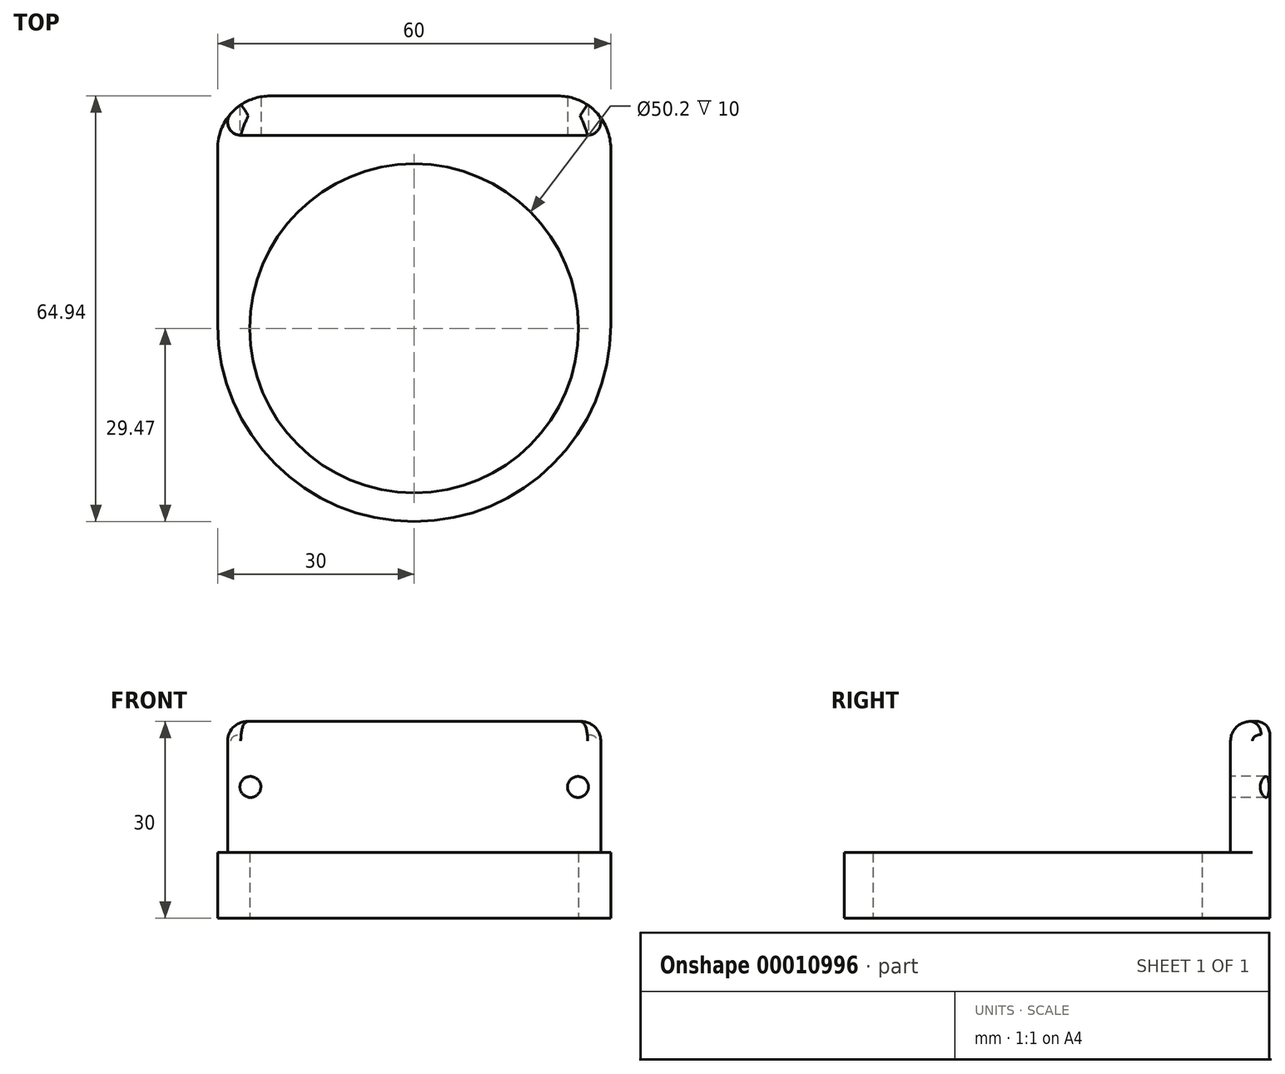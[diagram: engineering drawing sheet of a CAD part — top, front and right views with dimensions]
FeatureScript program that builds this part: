
annotation { "Feature Type Name" : "Feature", "Feature Type Description" : "" }
export const myFeature = defineFeature(function(context is Context, id is Id, definition is map)
    precondition{}
    {
        {
            var Q0;
            Q0=qCreatedBy(makeId("Top.planeOp"),FACE);
            var sketch = newSketch(context, id + "F0", { "sketchPlane" : qUnion([Q0])});
            skLineSegment(sketch, "E0.rect.bottom", {"start": v(-30, 29.47) * mm, "end": v(30, 29.47) * mm});
            skLineSegment(sketch, "E0.rect.top", {"start": v(-30, -29.47) * mm, "end": v(30, -29.47) * mm});
            skLineSegment(sketch, "E0.rect.left", {"start": v(-30, 29.47) * mm, "end": v(-30, -29.47) * mm});
            skLineSegment(sketch, "E0.rect.right", {"start": v(30, 29.47) * mm, "end": v(30, -29.47) * mm});
            skPoint(sketch, "E0.rect.middle", {"position": v(0, 0) * mm});
            skCircle(sketch, "E1", {"center": v(0, 0) * mm, "radius": 25.1 * mm});
            skSolve(sketch);
        }
        {
            var Q0;
            Q0 = qSketchRegion(id + "F0", true);
            extrude(context, id + "F1", {"entities" : qUnion([Q0]), "depth" : 10 * mm});
        }
        {
            var Q0;
            Q0=makeQuery(id+"F1.opExtrude","SWEPT_EDGE",EDGE,{"disambiguationData":[OSD([sQuery(id+"F0.wireOp",EDGE,"E0.rect.top"),sQuery(id+"F0.wireOp",EDGE,"E0.rect.left")])]});
            var Q1;
            Q1=makeQuery(id+"F1.opExtrude","SWEPT_EDGE",EDGE,{"disambiguationData":[OSD([sQuery(id+"F0.wireOp",EDGE,"E0.rect.top"),sQuery(id+"F0.wireOp",EDGE,"E0.rect.right")])]});
            fillet(context, id + "F2", {"entities" : qUnion([Q0, Q1]), "radius" : 30 * mm, "tangentPropagation" : true, "allowEdgeOverflow" : false});
        }
        {
            var Q0;
            Q0=makeQuery(id+"F1.opExtrude","SWEPT_FACE",FACE,{"disambiguationData":[OSD([sQuery(id+"F0.wireOp",EDGE,"E0.rect.bottom")])]});
            var sketch = newSketch(context, id + "F3", { "sketchPlane" : qUnion([Q0])});
            skLineSegment(sketch, "E2.rect.bottom", {"start": v(30, 0) * mm, "end": v(-30, 0) * mm});
            skLineSegment(sketch, "E2.rect.top", {"start": v(30, 30) * mm, "end": v(-30, 30) * mm});
            skLineSegment(sketch, "E2.rect.left", {"start": v(30, 0) * mm, "end": v(30, 30) * mm});
            skLineSegment(sketch, "E2.rect.right", {"start": v(-30, 0) * mm, "end": v(-30, 30) * mm});
            skPoint(sketch, "E2.rect.middle", {"position": v(0, 15) * mm});
            skCircle(sketch, "E3", {"center": v(-25, 20) * mm, "radius": 1.6 * mm});
            skCircle(sketch, "E4", {"center": v(25, 20) * mm, "radius": 1.6 * mm});
            skSolve(sketch);
        }
        {
            var Q0;
            Q0 = qSketchRegion(id + "F3", true);
            extrude(context, id + "F4", {"entities" : qUnion([Q0]), "operationType" : NewBodyOperationType.ADD, "depth" : 6 * mm});
        }
        {
            var Q0;
            Q0=makeQuery(id+"F4.opExtrude","CAP_EDGE",EDGE,{"disambiguationData":[OSD([sQuery(id+"F3.wireOp",EDGE,"E2.rect.top")])],"isStart":true});
            fillet(context, id + "F5", {"entities" : qUnion([Q0]), "radius" : 3 * mm, "allowEdgeOverflow" : false});
        }
        {
            var Q0;
            Q0=makeQuery(id+"F4.opExtrude","CAP_EDGE",EDGE,{"disambiguationData":[OSD([sQuery(id+"F3.wireOp",EDGE,"E2.rect.left")])],"isStart":false});
            var Q1;
            Q1=makeQuery(id+"F4.opExtrude","CAP_EDGE",EDGE,{"disambiguationData":[OSD([sQuery(id+"F3.wireOp",EDGE,"E2.rect.right")])],"isStart":false});
            fillet(context, id + "F6", {"entities" : qUnion([Q0, Q1]), "radius" : 8 * mm, "tangentPropagation" : true, "allowEdgeOverflow" : false});
        }
        {
            var Q0;
            {var subQ0=sQuery(id+"F3.wireOp",EDGE,"E2.rect.left");Q0=makeQuery(id+"F6.opFillet","BLEND_EDGE",EDGE,{"blendedFrom":[makeQuery(id+"F4.opExtrude","CAP_EDGE",EDGE,{"disambiguationData":[OSD([subQ0])],"isStart":false}),makeQuery(id+"F4.opExtrude","CAP_FACE",FACE,{"disambiguationData":[OSD([sQuery(id+"F3.wireOp",EDGE,"E2.rect.bottom"),sQuery(id+"F3.wireOp",EDGE,"E2.rect.top"),subQ0,sQuery(id+"F3.wireOp",EDGE,"E2.rect.right")])],"isStart":true})],"blendedInto":[makeQuery(id+"F4.opExtrude","CAP_FACE",FACE,{"disambiguationData":[OSD([sQuery(id+"F3.wireOp",EDGE,"E2.rect.bottom"),sQuery(id+"F3.wireOp",EDGE,"E2.rect.top"),subQ0,sQuery(id+"F3.wireOp",EDGE,"E2.rect.right")])],"isStart":true})]});}
            var Q1;
            {var subQ0=sQuery(id+"F3.wireOp",EDGE,"E2.rect.right");Q1=makeQuery(id+"F6.opFillet","BLEND_EDGE",EDGE,{"blendedFrom":[makeQuery(id+"F4.opExtrude","CAP_EDGE",EDGE,{"disambiguationData":[OSD([subQ0])],"isStart":false}),makeQuery(id+"F4.opExtrude","CAP_FACE",FACE,{"disambiguationData":[OSD([sQuery(id+"F3.wireOp",EDGE,"E2.rect.bottom"),sQuery(id+"F3.wireOp",EDGE,"E2.rect.top"),sQuery(id+"F3.wireOp",EDGE,"E2.rect.left"),subQ0])],"isStart":true})],"blendedInto":[makeQuery(id+"F4.opExtrude","CAP_FACE",FACE,{"disambiguationData":[OSD([sQuery(id+"F3.wireOp",EDGE,"E2.rect.bottom"),sQuery(id+"F3.wireOp",EDGE,"E2.rect.top"),sQuery(id+"F3.wireOp",EDGE,"E2.rect.left"),subQ0])],"isStart":true})]});}
            fillet(context, id + "F7", {"entities" : qUnion([Q0, Q1]), "radius" : 2 * mm, "tangentPropagation" : true, "allowEdgeOverflow" : false});
        }
    });
